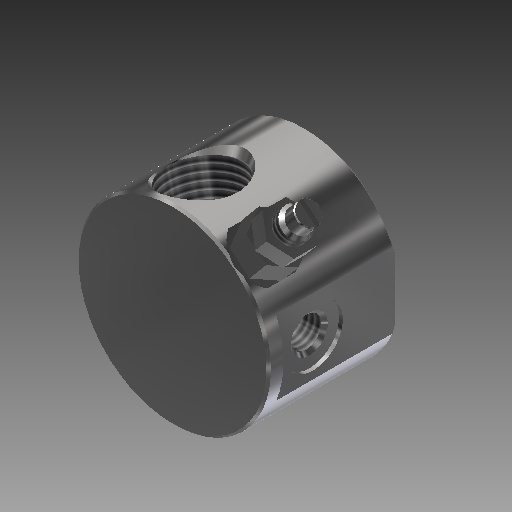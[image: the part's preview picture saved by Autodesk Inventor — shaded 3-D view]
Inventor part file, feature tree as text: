
AUTODESK INVENTOR PART (.ipt)
format: ipt  version: 2018 (Build 220112000, 112)  size: 323,072 bytes
history: native  units: in
note: dims shown in document units (in); Inventor stores cm internally (conversion verified against a paired STEP export)
features: other x35, sketch x14, revolve x5, extrude x5, hole x4, thread x4
ambient origin geometry x8: Origin, YZ Plane, XZ Plane, XY Plane, X Axis, Y Axis, Z Axis, Center Point
bodies: Solid1 (feature_tree)
feature tree (67):
  revolve  "Revolution1"  [1 undecoded]
  hole  "Hole1"  [1 undecoded]
  hole  "Hole2"  [1 undecoded]
  hole  "Hole3"  [1 undecoded]
  hole  "Hole4"  [1 undecoded]
  extrude  "Extrusion1"  Depth=0.252in TaperAngle=0.0deg
  revolve  "Revolution2"  [1 undecoded]
  thread  "Thread1"  [1 undecoded]
  revolve  "Revolution3"  [1 undecoded]
  thread  "Thread2"  [1 undecoded]
  extrude  "Extrusion2"  [1 undecoded]
  extrude  "Extrusion3"  [1 undecoded]
  extrude  "Extrusion4"  [1 undecoded]
  revolve  "Revolution4"  [1 undecoded]
  thread  "Thread3"  [1 undecoded]
  extrude  "Extrusion5"  [1 undecoded]
  revolve  "Revolution5"  [1 undecoded]
  thread  "Thread4"  [1 undecoded]
  other  "conn_XY"
  other  "conn_YZ"
  other  "conn_ZX"
  other  "conn_X"
  other  "conn_Y"
  other  "conn_Z"
  other  "conn_Center"
  other  "conn2_XY"
  other  "conn2_YZ"
  other  "conn2_ZX"
  other  "conn2_X"
  other  "conn2_Y"
  other  "conn2_Z"
  other  "conn2_Center"
  other  "mnt_XY"
  other  "mnt_YZ"
  other  "mnt_ZX"
  other  "mnt_X"
  other  "mnt_Y"
  other  "mnt_Z"
  other  "mnt_Center"
  other  "trun1_XY"
  other  "trun1_YZ"
  other  "trun1_ZX"
  other  "trun1_X"
  other  "trun1_Y"
  other  "trun1_Z"
  other  "trun1_Center"
  other  "trun2_XY"
  other  "trun2_YZ"
  other  "trun2_ZX"
  other  "trun2_X"
  other  "trun2_Y"
  other  "trun2_Z"
  other  "trun2_Center"
  sketch  "Sketch_3"  dims[d1=0.134in d2=0.28in d3=0.164in d4=0.25in d5=90.0deg d6=0.28in d7=0.8383in]
  sketch  "Sketch2"  dims[d0=360.0deg]
  sketch  "Sketch3"  dims[d8=0.134in d9=0.28in d10=0.164in d11=0.25in d12=90.0deg d13=0.28in d14=0.8383in]
  sketch  "Sketch4"  dims[d15=0.134in d16=0.28in d17=0.164in d18=0.25in d19=90.0deg d20=0.28in d21=0.8383in]
  sketch  "Sketch5"  dims[d22=0.134in d23=0.28in d24=0.164in d25=0.25in d26=90.0deg d27=0.28in d28=0.8383in d29=0.63in d30=0.0in]
  sketch  "Sketch_6"  dims[d31=360.0deg d32=0.1399in d33=0.0in]
  sketch  "Sketch_7"  dims[d34=360.0deg d35=0.1399in d36=0.0in]
  sketch  "Sketch_8"  dims[d37=0.138in d38=0.0in d39=0.138in d40=0.0in]
  sketch  "Sketch_13"
  sketch  "Sketch_14"
  sketch  "Sketch_15"
  sketch  "Sketch_9"  dims[d41=0.094in d42=0.0in d43=360.0deg]
  sketch  "Sketch_11"  dims[d48=360.0deg d49=0.2731in d50=0.0in d51=0.0in d52=0.0in d53=0.0in d54=0.0in]
  sketch  "Sketch_10"  dims[d44=0.0573in d45=0.0in d46=0.252in d47=0.0in]
note: 17 required parameter values undecoded (feature->parameter linkage not recoverable at this tier; creation-order binding heuristic only, values carry confidence <= 0.55)